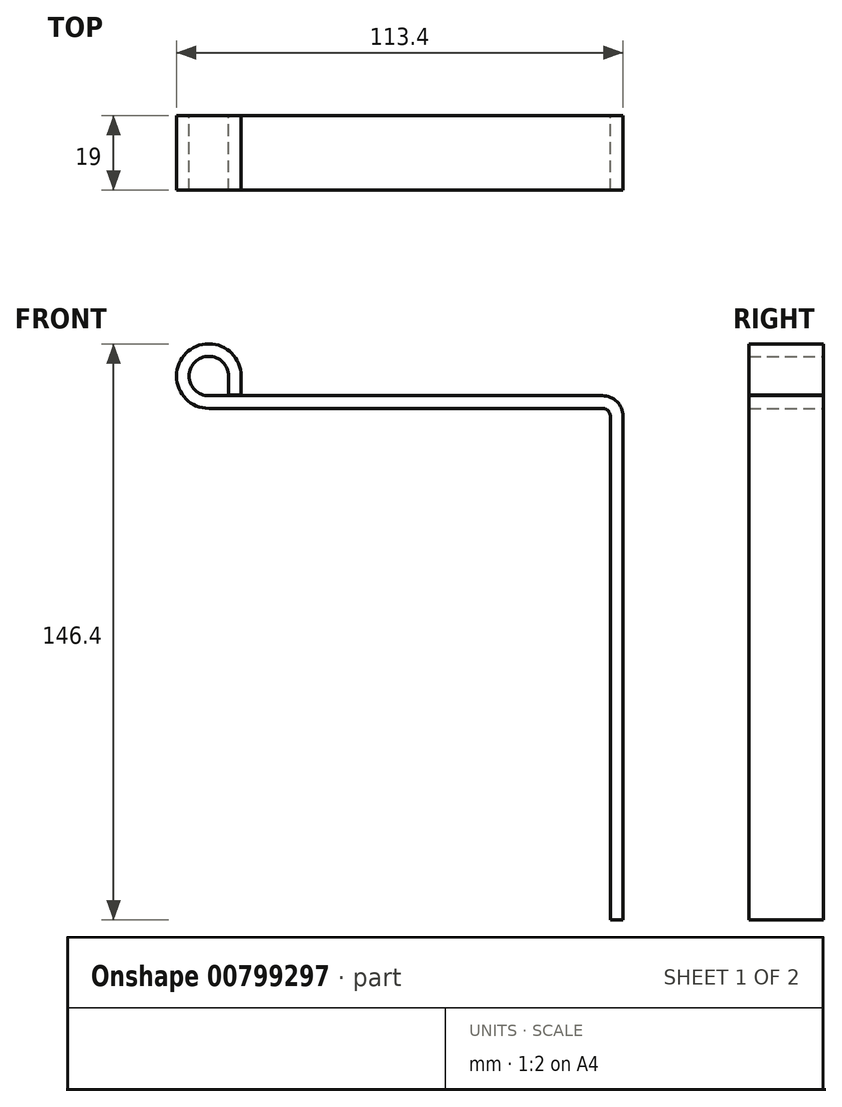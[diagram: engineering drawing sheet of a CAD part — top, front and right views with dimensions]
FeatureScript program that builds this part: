
annotation { "Feature Type Name" : "Feature", "Feature Type Description" : "" }
export const myFeature = defineFeature(function(context is Context, id is Id, definition is map)
    precondition{}
    {
        {
            var Q0;
            Q0=qCreatedBy(makeId("Front.planeOp"),FACE);
            var sketch = newSketch(context, id + "F0", { "sketchPlane" : qUnion([Q0]), "disableImprinting" : false});
            skArc(sketch, "E0", {"start": v(5, 0) * mm, "mid": v(-3.54, 3.54) * mm, "end": v(0, -5) * mm});
            skArc(sketch, "E1", {"start": v(8.2, 0) * mm, "mid": v(-5.8, 5.8) * mm, "end": v(0, -8.2) * mm});
            skLineSegment(sketch, "E2.right", {"start": v(8.2, 0) * mm, "end": v(8.2, -4.8) * mm});
            skLineSegment(sketch, "E3.left", {"start": v(5, 0) * mm, "end": v(5, -4.8) * mm});
            skLineSegment(sketch, "E4", {"start": v(5, -4.8) * mm, "end": v(8.2, -4.8) * mm});
            skLineSegment(sketch, "E5", {"start": v(0, -5) * mm, "end": v(100, -5) * mm});
            skLineSegment(sketch, "E6", {"start": v(0, -8.2) * mm, "end": v(100, -8.2) * mm});
            skLineSegment(sketch, "E7.bottom", {"start": v(102, -138.2) * mm, "end": v(105.23, -138.2) * mm});
            skArc(sketch, "E8", {"start": v(102, -10.2) * mm, "mid": v(101.41, -8.79) * mm, "end": v(100, -8.2) * mm});
            skArc(sketch, "E9", {"start": v(105.2, -10.2) * mm, "mid": v(103.68, -6.52) * mm, "end": v(100, -5) * mm});
            skLineSegment(sketch, "E10.top", {"start": v(105.2, -138.2) * mm, "end": v(102, -138.2) * mm});
            skLineSegment(sketch, "E10.left", {"start": v(105.2, -10.2) * mm, "end": v(105.2, -138.2) * mm});
            skLineSegment(sketch, "E10.right", {"start": v(102, -10.2) * mm, "end": v(102, -138.2) * mm});
            skSolve(sketch);
        }
        {
            var Q0;
            Q0 = qSketchRegion(id + "F0", true);
            extrude(context, id + "F1", {"entities" : qUnion([Q0]), "depth" : 19 * mm, "offsetDistance" : 25 * mm});
        }
    });
